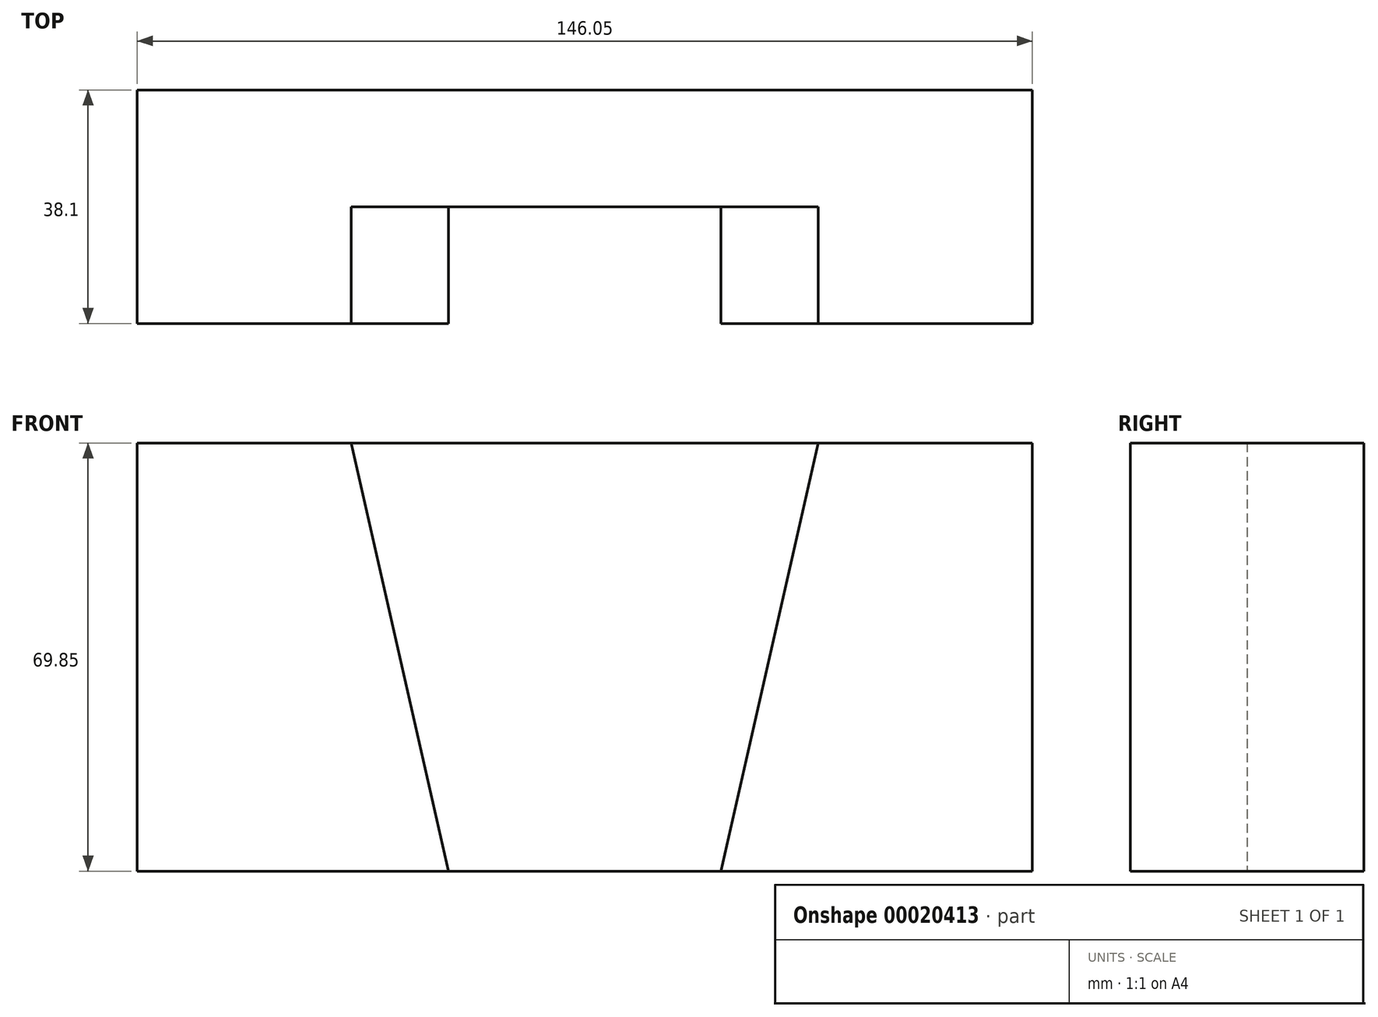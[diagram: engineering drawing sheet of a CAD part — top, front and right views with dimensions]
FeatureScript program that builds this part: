
annotation { "Feature Type Name" : "Feature", "Feature Type Description" : "" }
export const myFeature = defineFeature(function(context is Context, id is Id, definition is map)
    precondition{}
    {
        {
            var Q0;
            Q0=qCreatedBy(makeId("Front.planeOp"),FACE);
            var sketch = newSketch(context, id + "F0", { "sketchPlane" : qUnion([Q0])});
            skLineSegment(sketch, "E0.bottom", {"start": v(-78.22, 28.22) * mm, "end": v(67.83, 28.22) * mm});
            skLineSegment(sketch, "E0.top", {"start": v(-78.22, -41.63) * mm, "end": v(67.83, -41.63) * mm});
            skLineSegment(sketch, "E0.left", {"start": v(-78.22, 28.22) * mm, "end": v(-78.22, -41.63) * mm});
            skLineSegment(sketch, "E0.right", {"start": v(67.83, 28.22) * mm, "end": v(67.83, -41.63) * mm});
            skLineSegment(sketch, "E1", {"start": v(-43.3, 28.22) * mm, "end": v(-27.42, -41.63) * mm});
            skLineSegment(sketch, "E2", {"start": v(32.9, 28.22) * mm, "end": v(17.03, -41.63) * mm});
            skSolve(sketch);
        }
        {
            var Q0;
            {var subQ1=sQuery(id+"F0.wireOp",EDGE,"E0.left");Q0=makeQuery(id+"F0.imprint","IMPRINT",FACE,{"disambiguationData":[TD([[makeQuery(id+"F0.imprint","IMPRINT",EDGE,{"derivedFrom":subQ1}),1.0]])]});}
            extrude(context, id + "F1", {"entities" : qUnion([Q0]), "depth" : 38.1 * mm});
        }
        {
            var Q0;
            {var subQ1=sQuery(id+"F0.wireOp",EDGE,"E1");Q0=makeQuery(id+"F0.imprint","IMPRINT",FACE,{"disambiguationData":[TD([[makeQuery(id+"F0.imprint","IMPRINT",EDGE,{"derivedFrom":subQ1}),1.0]])]});}
            extrude(context, id + "F2", {"entities" : qUnion([Q0]), "operationType" : NewBodyOperationType.ADD, "depth" : 19.05 * mm});
        }
        {
            var Q0;
            {var subQ1=sQuery(id+"F0.wireOp",EDGE,"E0.right");Q0=makeQuery(id+"F0.imprint","IMPRINT",FACE,{"disambiguationData":[TD([[makeQuery(id+"F0.imprint","IMPRINT",EDGE,{"derivedFrom":subQ1}),-1.0]])]});}
            extrude(context, id + "F3", {"entities" : qUnion([Q0]), "operationType" : NewBodyOperationType.ADD, "depth" : 38.1 * mm});
        }
    });
